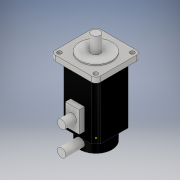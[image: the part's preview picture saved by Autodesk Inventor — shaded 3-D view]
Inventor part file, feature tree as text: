
AUTODESK INVENTOR PART (.ipt)
format: ipt  version: 2019.4 (Build 234330000, 330)  size: 246,272 bytes
history: native  units: mm
features: sketch x12, extrude x9, fillet x1, plane x1
ambient origin geometry x8: Origin, YZ Plane, XZ Plane, XY Plane, X Axis, Y Axis, Z Axis, Center Point
bodies: Solid1 (feature_tree)
feature tree (23):
  extrude  "Extrusion1"  Depth=34.0mm
  sketch  "Sketch4"  dims[d2=54.0mm d3=0.0mm d15=4.0mm]
  extrude  "Extrusion2"  Depth=4.0mm
  extrude  "Extrusion3"  Depth=4.0mm
  extrude  "Extrusion4"  Depth=5.0mm TaperAngle=0.0deg
  extrude  "Extrusion5"  TaperAngle=0.0deg  [1 undecoded]
  extrude  "Extrusion6"  Depth=17.0mm
  fillet  "Fillet1"  Radius=40.0mm
  extrude  "Extrusion7"  Depth=21.0mm
  plane  "Work Plane1"
  sketch  "Sketch12"  dims[d44=8.0mm d45=3.75mm]
  extrude  "Extrusion8"  Depth=1.0mm TaperAngle=0.0deg
  sketch  "Sketch14"  dims[d48=4.0mm]
  extrude  "Extrusion9"  Depth=3.75mm
  sketch  "Sketch1"  dims[d0=34.0mm d1=34.0mm]
  sketch  "Sketch5"  dims[d16=5.0mm d17=0.0mm d18=4.0mm]
  sketch  "Sketch6"  dims[d19=20.0mm d21=34.0mm d22=20.0mm d24=34.0mm d27=5.0mm d28=0.0mm]
  sketch  "Sketch8"  dims[d29=4.0mm d31=0.0mm]
  sketch  "Sketch9"  dims[d32=3.0mm d33=17.0mm d34=40.0mm d36=360.0deg]
  sketch  "Sketch10"  dims[d38=5.0mm d39=0.0mm d40=21.0mm]
  sketch  "Sketch11"  dims[d41=30.0mm d42=1.0mm d43=0.0mm]
  sketch  "Sketch13"  dims[d46=15.0mm d47=0.0mm]
  sketch  "Sketch15"  dims[d49=17.0mm d50=13.0mm d51=20.0mm d52=5.0mm d53=0.0mm d54=15.0mm d57=17.0mm d58=30.0mm d59=12.0mm d60=0.0mm d61=8.0mm d62=8.0mm d63=6.5mm d64=8.0mm d65=23.0mm d66=8.0mm d67=20.0mm d68=0.0mm]
note: 1 required parameter value undecoded (feature->parameter linkage not recoverable at this tier; creation-order binding heuristic only, values carry confidence <= 0.55)
